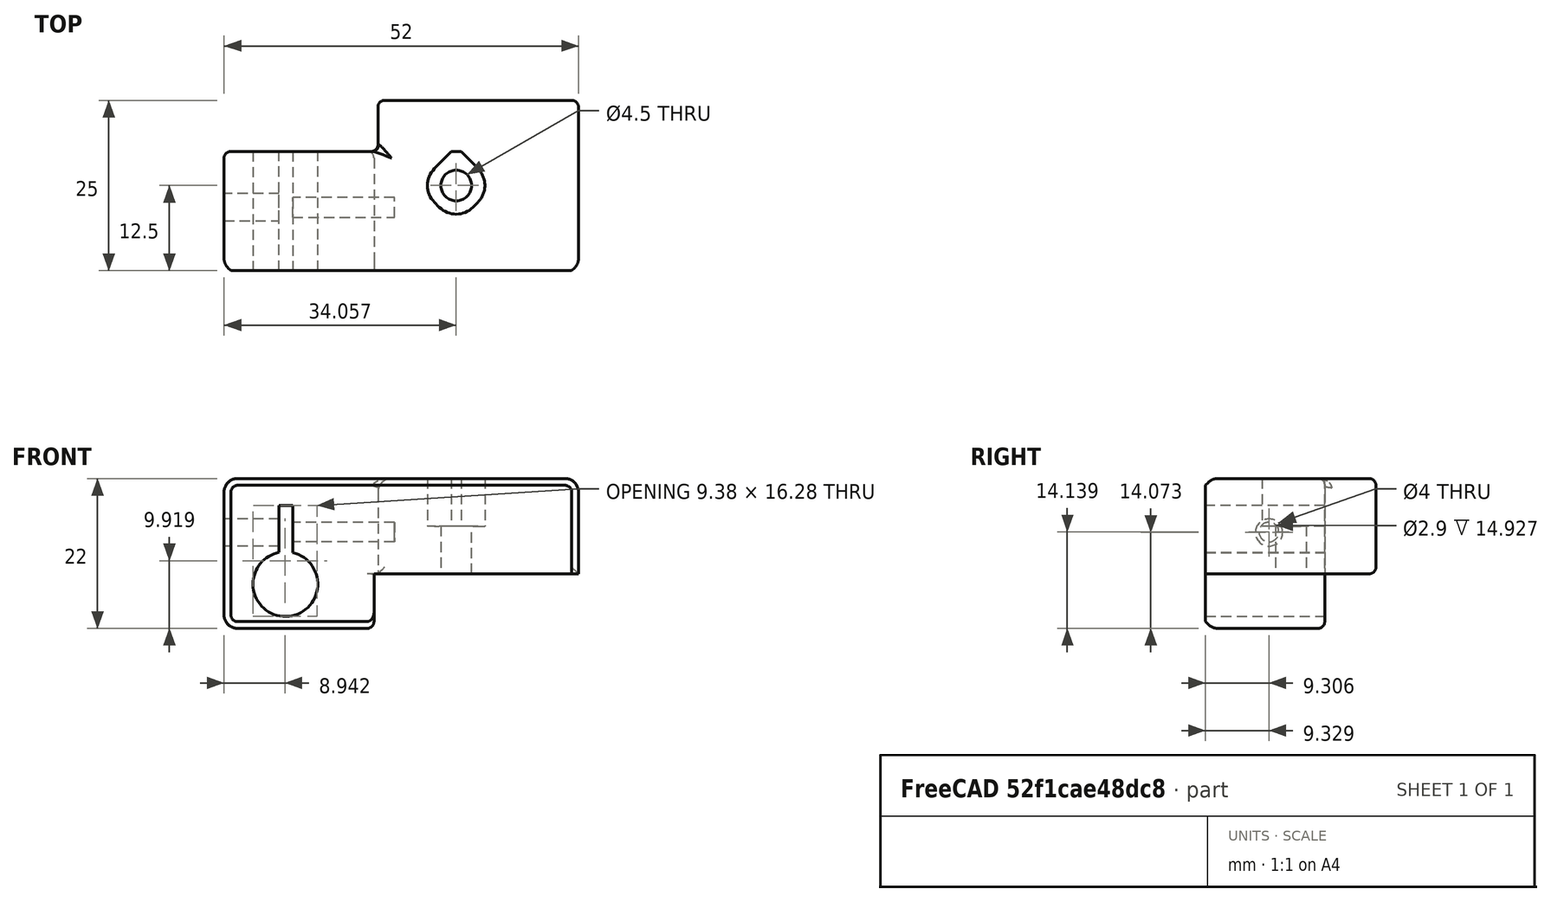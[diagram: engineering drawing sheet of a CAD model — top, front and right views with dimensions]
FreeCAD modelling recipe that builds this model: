
FCSTD DOCUMENT  (FreeCAD 0.19R)
Label: MicrometerMount2
License: All rights reserved
LicenseURL: http://en.wikipedia.org/wiki/All_rights_reserved
objects: Sketcher::SketchObject×9, PartDesign::Pocket×8, PartDesign::Fillet×7, PartDesign::Chamfer×2, PartDesign::Pad×1, PartDesign::Body×1, Mesh::Feature×1
note: 46 computed .brp shape members not serialized (recipe doc carries the construction recipe); baked Part::Feature solids carry a one-line shape summary decoded from their .brp

FEATURE [Sketcher::SketchObject] Sketch
  FullyConstrained = true
  MapMode = 5
  Support = -> [XY_Plane]
  sketch-geometry (4):
    g0: LineSegment StartX=-26 StartY=12.5 StartZ=0 EndX=26 EndY=12.5 EndZ=0
    g1: LineSegment StartX=26 StartY=12.5 StartZ=0 EndX=26 EndY=-12.5 EndZ=0
    g2: LineSegment StartX=26 StartY=-12.5 StartZ=0 EndX=-26 EndY=-12.5 EndZ=0
    g3: LineSegment StartX=-26 StartY=-12.5 StartZ=0 EndX=-26 EndY=12.5 EndZ=0
  constraints (11):
    c: Coincident(g0,g1)
    c: Coincident(g1,g2)
    c: Coincident(g2,g3)
    c: Coincident(g3,g0)
    c: Horizontal(g0)
    c: Horizontal(g2)
    c: Vertical(g3)
    c: Distance(g0) = 52
    c: Distance(g1) = 25
    c: Symmetric(g0,g2,g-1)
    c: Vertical(g1)
FEATURE [PartDesign::Pad] Pad
  Direction = (1,1,1)
  Length = 22
  Length2 = 100
  Profile = -> Sketch
  Type = 0
FEATURE [Sketcher::SketchObject] Sketch001
  FullyConstrained = true
  MapMode = 5
  Placement = pos=(0,12.5,0) rot=(0,0.707107,0.707107;3.14159rad)
  Support = -> [Pad]
  sketch-geometry (1):
    g0: Circle CenterX=17 CenterY=6.5 CenterZ=0 NormalX=0 NormalY=0 NormalZ=1 AngleXU=0 Radius=4.75
  constraints (3):
    c: Diameter(g0) = 9.5
    c: DistanceY(g0) = 6.5
    c: DistanceX(g0) = 17
FEATURE [PartDesign::Pocket] Pocket
  BaseFeature = -> Pad
  Length = 5
  Length2 = 100
  Profile = -> Sketch001
  Type = 1
FEATURE [Sketcher::SketchObject] Sketch002
  FullyConstrained = false
  MapMode = 5
  Placement = pos=(0,12.5,0) rot=(0,0.707107,0.707107;3.14159rad)
  Support = -> [Pocket]
  sketch-geometry (4):
    g0: LineSegment StartX=15.9267 StartY=18.0597 StartZ=0 EndX=17.9267 EndY=18.0597 EndZ=0
    g1: LineSegment StartX=17.9267 StartY=18.0597 StartZ=0 EndX=17.9267 EndY=6.00734 EndZ=0
    g2: LineSegment StartX=17.9267 StartY=6.00734 StartZ=0 EndX=15.9267 EndY=6.00734 EndZ=0
    g3: LineSegment StartX=15.9267 StartY=6.00734 StartZ=0 EndX=15.9267 EndY=18.0597 EndZ=0
  constraints (9):
    c: Coincident(g0,g1)
    c: Coincident(g1,g2)
    c: Coincident(g2,g3)
    c: Coincident(g3,g0)
    c: Horizontal(g0)
    c: Horizontal(g2)
    c: Vertical(g1)
    c: Vertical(g3)
    c: Distance(g0) = 2
FEATURE [PartDesign::Pocket] Pocket001
  BaseFeature = -> Pocket
  Length = 5
  Length2 = 100
  Profile = -> Sketch002
  Type = 1
FEATURE [Sketcher::SketchObject] Sketch003
  FullyConstrained = false
  MapMode = 5
  Placement = pos=(-26,0,0) rot=(0.57735,-0.57735,-0.57735;2.0944rad)
  Support = -> [Pocket001]
  sketch-geometry (1):
    g0: Circle CenterX=3.19376 CenterY=14.1394 CenterZ=0 NormalX=0 NormalY=0 NormalZ=1 AngleXU=0 Radius=1.45
  constraints (1):
    c: Diameter(g0) = 2.9
FEATURE [PartDesign::Pocket] Pocket002
  BaseFeature = -> Pocket001
  Length = 25
  Length2 = 100
  Profile = -> Sketch003
  Type = 0
FEATURE [Sketcher::SketchObject] Sketch004
  FullyConstrained = false
  MapMode = 5
  Placement = pos=(0,12.5,0) rot=(0,0.707107,0.707107;3.14159rad)
  Support = -> [Pocket002]
  sketch-geometry (4):
    g0: LineSegment StartX=-29.2865 StartY=8 StartZ=0 EndX=4 EndY=8 EndZ=0
    g1: LineSegment StartX=4 StartY=8 StartZ=0 EndX=4 EndY=-7.88958 EndZ=0
    g2: LineSegment StartX=4 StartY=-7.88958 StartZ=0 EndX=-29.2865 EndY=-7.88958 EndZ=0
    g3: LineSegment StartX=-29.2865 StartY=-7.88958 StartZ=0 EndX=-29.2865 EndY=8 EndZ=0
  constraints (10):
    c: Coincident(g0,g1)
    c: Coincident(g1,g2)
    c: Coincident(g2,g3)
    c: Coincident(g3,g0)
    c: Horizontal(g0)
    c: Horizontal(g2)
    c: Vertical(g1)
    c: Vertical(g3)
    c: DistanceY(g0) = 8
    c: DistanceX(g0) = 4
FEATURE [PartDesign::Pocket] Pocket003
  BaseFeature = -> Pocket002
  Length = 5
  Length2 = 100
  Profile = -> Sketch004
  Type = 1
FEATURE [Sketcher::SketchObject] Sketch007
  FullyConstrained = false
  MapMode = 5
  Placement = pos=(0,0,22) rot=(0,0,1;0rad)
  Support = -> [Pocket003]
  sketch-geometry (4):
    g0: LineSegment StartX=-31.1591 StartY=25.1381 StartZ=0 EndX=-3.42363 EndY=25.1381 EndZ=0
    g1: LineSegment StartX=-3.42363 StartY=25.1381 StartZ=0 EndX=-3.42363 EndY=5 EndZ=0
    g2: LineSegment StartX=-3.42363 StartY=5 StartZ=0 EndX=-31.1591 EndY=5 EndZ=0
    g3: LineSegment StartX=-31.1591 StartY=5 StartZ=0 EndX=-31.1591 EndY=25.1381 EndZ=0
  constraints (9):
    c: Coincident(g0,g1)
    c: Coincident(g1,g2)
    c: Coincident(g2,g3)
    c: Coincident(g3,g0)
    c: Horizontal(g0)
    c: Horizontal(g2)
    c: Vertical(g1)
    c: Vertical(g3)
    c: DistanceY(g1) = 5
FEATURE [PartDesign::Pocket] Pocket004
  BaseFeature = -> Pocket003
  Length = 5
  Length2 = 100
  Profile = -> Sketch007
  Type = 1
FEATURE [Sketcher::SketchObject] Sketch011
  FullyConstrained = false
  MapMode = 5
  Placement = pos=(0,0,22) rot=(0,0,1;0rad)
  Support = -> [Pocket004]
  sketch-geometry (4):
    g0: LineSegment StartX=8.05657 StartY=5.65685 StartZ=0 EndX=2.39971 EndY=9.8e-15 EndZ=0
    g1: LineSegment StartX=2.39971 StartY=9.8e-15 StartZ=0 EndX=8.05657 EndY=-5.65685 EndZ=0
    g2: LineSegment StartX=8.05657 StartY=-5.65685 StartZ=0 EndX=13.7134 EndY=0 EndZ=0
    g3: LineSegment StartX=13.7134 StartY=0 StartZ=0 EndX=8.05657 EndY=5.65685 EndZ=0
  constraints (10):
    c: Coincident(g0,g1)
    c: Coincident(g1,g2)
    c: Coincident(g2,g3)
    c: Coincident(g3,g0)
    c: Perpendicular(g3,g0)
    c: Perpendicular(g0,g1)
    c: Perpendicular(g3,g2)
    c: Equal(g3,g0)
    c: PointOnObject(g2,g-1)
    c: Distance(g3) = 8
FEATURE [PartDesign::Pocket] Pocket005
  BaseFeature = -> Pocket004
  Length = 7
  Length2 = 100
  Profile = -> Sketch011
  Type = 0
FEATURE [Sketcher::SketchObject] Sketch009
  FullyConstrained = false
  MapMode = 5
  Placement = pos=(0,1.8e-15,8) rot=(1,0,0;3.14159rad)
  Support = -> [Pocket005]
  sketch-geometry (1):
    g0: Circle CenterX=8.05657 CenterY=0 CenterZ=0 NormalX=0 NormalY=0 NormalZ=1 AngleXU=0 Radius=2.25
  constraints (2):
    c: PointOnObject(g0,g-1)
    c: Diameter(g0) = 4.5
FEATURE [PartDesign::Pocket] Pocket006
  BaseFeature = -> Pocket005
  Length = 5
  Length2 = 100
  Profile = -> Sketch009
  Type = 1
FEATURE [Sketcher::SketchObject] Sketch005
  FullyConstrained = false
  MapMode = 5
  Placement = pos=(-26,0,0) rot=(0.57735,-0.57735,-0.57735;2.0944rad)
  Support = -> [Pocket006]
  sketch-geometry (1):
    g0: Circle CenterX=3.17131 CenterY=14.0734 CenterZ=0 NormalX=0 NormalY=0 NormalZ=1 AngleXU=0 Radius=2
  constraints (1):
    c: Diameter(g0) = 4
FEATURE [PartDesign::Pocket] Pocket007
  BaseFeature = -> Pocket006
  Length = 10
  Length2 = 100
  Profile = -> Sketch005
  Type = 0
FEATURE [PartDesign::Fillet] Fillet
  Base = -> Pocket007 [Edge16,Edge41,Edge5,Edge14]
  BaseFeature = -> Pocket007
  Radius = 2
  SupportTransform = false
FEATURE [PartDesign::Fillet] Fillet001
  Base = -> Fillet [Face1]
  BaseFeature = -> Fillet
  Radius = 1
  SupportTransform = false
FEATURE [PartDesign::Fillet] Fillet002
  Base = -> Fillet001 [Edge42]
  BaseFeature = -> Fillet001
  Radius = 1
  SupportTransform = false
FEATURE [PartDesign::Chamfer] Chamfer
  Angle = 45
  Base = -> Fillet002 [Edge27]
  BaseFeature = -> Fillet002
  ChamferType = 0
  FlipDirection = false
  Size = 1
  Size2 = 1
  SupportTransform = false
FEATURE [PartDesign::Fillet] Fillet003
  Base = -> Chamfer [Edge2]
  BaseFeature = -> Chamfer
  Radius = 2
  SupportTransform = false
FEATURE [PartDesign::Chamfer] Chamfer001
  Angle = 45
  Base = -> Fillet003 [Edge34]
  BaseFeature = -> Fillet003
  ChamferType = 0
  FlipDirection = false
  Size = 1
  Size2 = 1
  SupportTransform = false
FEATURE [PartDesign::Fillet] Fillet004
  Base = -> Chamfer001 [Edge15,Edge19,Edge21]
  BaseFeature = -> Chamfer001
  Radius = 3.5
  SupportTransform = false
FEATURE [PartDesign::Fillet] Fillet005
  Base = -> Fillet004 [Edge120]
  BaseFeature = -> Fillet004
  Radius = 1
  SupportTransform = false
FEATURE [PartDesign::Fillet] Fillet006
  Base = -> Fillet005 [Edge8]
  BaseFeature = -> Fillet005
  Radius = 1
  SupportTransform = false
FEATURE [PartDesign::Body] Body
  Group = -> [Sketch,Pad,Sketch001,Pocket,Sketch002,Pocket001,Sketch003,Pocket002,Sketch004,Pocket003,Sketch005,Sketch007,Sketch009,Sketch011,Pocket004,Pocket005,Pocket006,Pocket007,Fillet,Fillet001,Fillet002,Chamfer,Fillet003,Chamfer001,Fillet004,Fillet005,Fillet006]
  Origin = -> Origin
  Tip = -> Fillet006
FEATURE [Mesh::Feature] Mesh  label="Fillet006 (Meshed)"
